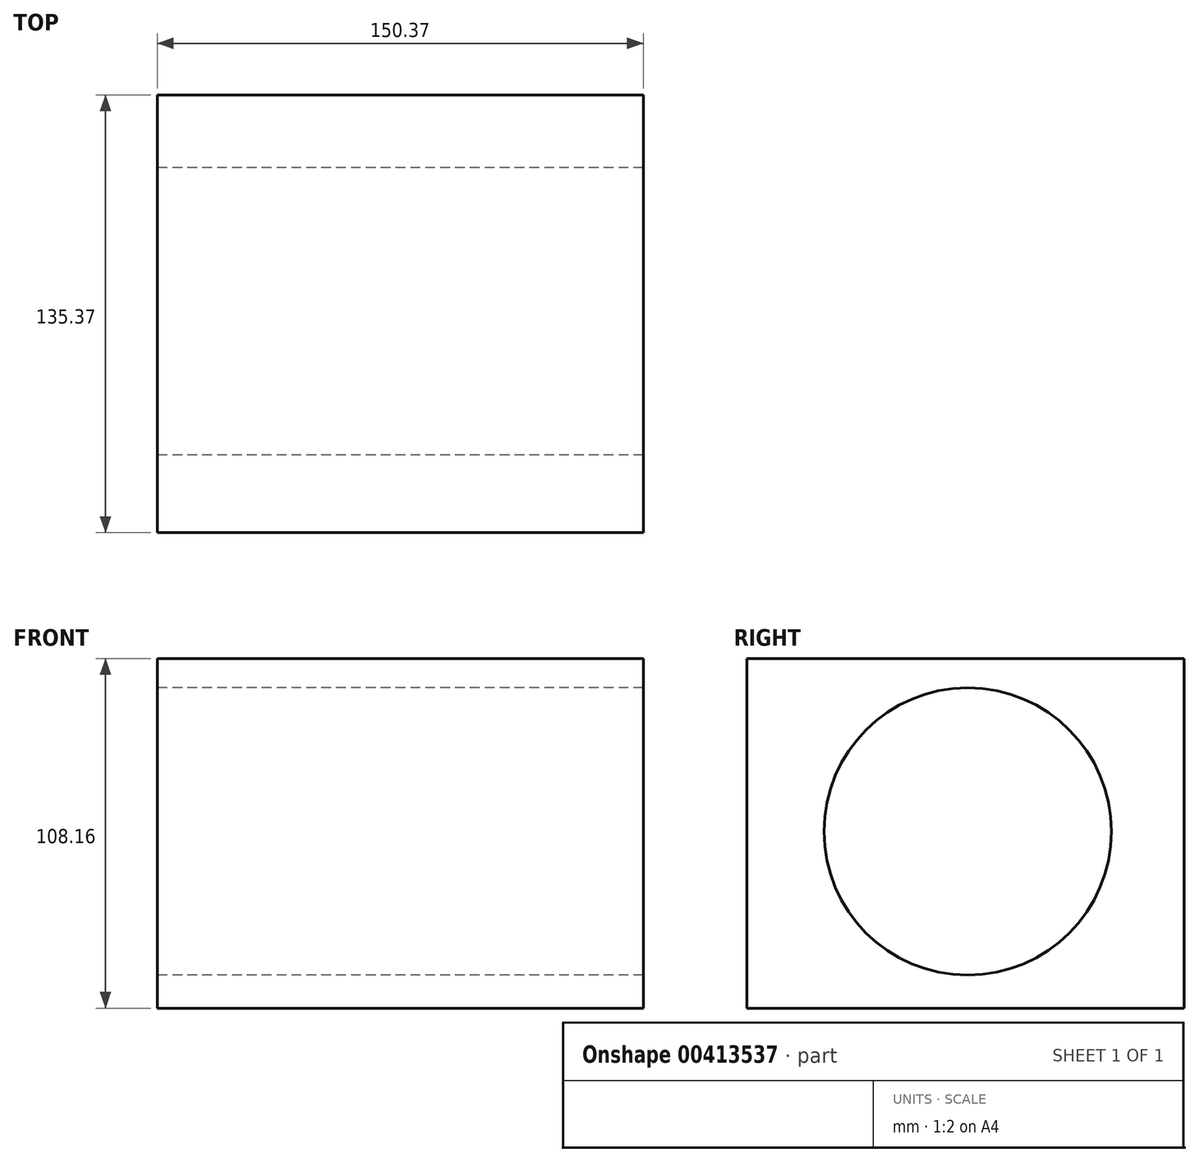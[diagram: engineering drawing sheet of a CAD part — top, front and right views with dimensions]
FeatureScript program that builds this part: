
annotation { "Feature Type Name" : "Feature", "Feature Type Description" : "" }
export const myFeature = defineFeature(function(context is Context, id is Id, definition is map)
    precondition{}
    {
        {
            var Q0;
            Q0=qCreatedBy(makeId("Right.planeOp"),FACE);
            var sketch = newSketch(context, id + "F0", { "sketchPlane" : qUnion([Q0])});
            skCircle(sketch, "E0", {"center": v(0, 0) * mm, "radius": 44.46 * mm});
            skLineSegment(sketch, "E1.bottom", {"start": v(66.99, 53.5) * mm, "end": v(-68.38, 53.5) * mm});
            skLineSegment(sketch, "E1.top", {"start": v(66.99, -54.66) * mm, "end": v(-68.38, -54.66) * mm});
            skLineSegment(sketch, "E1.left", {"start": v(66.99, 53.5) * mm, "end": v(66.99, -54.66) * mm});
            skLineSegment(sketch, "E1.right", {"start": v(-68.38, 53.5) * mm, "end": v(-68.38, -54.66) * mm});
            skSolve(sketch);
        }
        {
            var Q0;
            Q0=makeQuery(id+"F0.imprint","IMPRINT",FACE,{"disambiguationData":[TD([[makeQuery(id+"F0.imprint","IMPRINT",EDGE,{"derivedFrom":sQuery(id+"F0.wireOp",EDGE,"E0")}),-1.0]])]});
            extrude(context, id + "F1", {"entities" : qUnion([Q0]), "depth" : 150.37 * mm});
        }
    });
